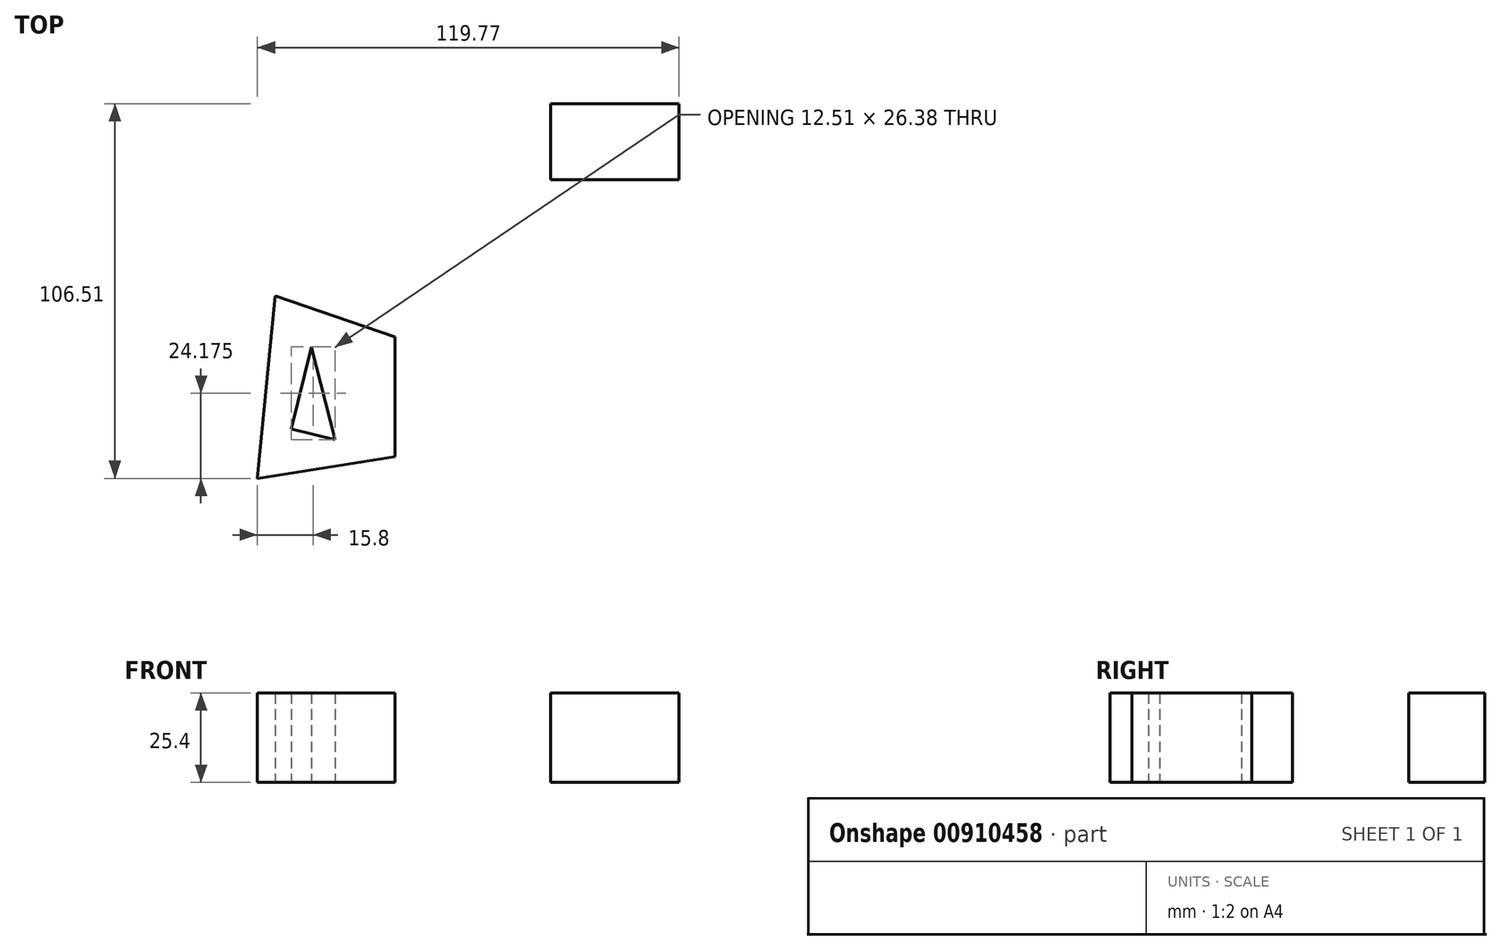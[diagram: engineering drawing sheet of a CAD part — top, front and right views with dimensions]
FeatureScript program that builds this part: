
annotation { "Feature Type Name" : "Feature", "Feature Type Description" : "" }
export const myFeature = defineFeature(function(context is Context, id is Id, definition is map)
    precondition{}
    {
        {
            var Q0;
            Q0=qCreatedBy(makeId("Top.planeOp"),FACE);
            var sketch = newSketch(context, id + "F0", { "sketchPlane" : qUnion([Q0])});
            skCircle(sketch, "E0", {"center": v(-62.28, 52.52) * mm, "radius": 11.18 * mm});
            skLineSegment(sketch, "E1.bottom", {"start": v(23.25, 37.16) * mm, "end": v(59.79, 37.16) * mm});
            skLineSegment(sketch, "E1.top", {"start": v(23.25, 15.57) * mm, "end": v(59.79, 15.57) * mm});
            skLineSegment(sketch, "E1.left", {"start": v(23.25, 37.16) * mm, "end": v(23.25, 15.57) * mm});
            skLineSegment(sketch, "E1.right", {"start": v(59.79, 37.16) * mm, "end": v(59.79, 15.57) * mm});
            skLineSegment(sketch, "E2", {"start": v(-55, -17.45) * mm, "end": v(-20.95, -29.08) * mm});
            skLineSegment(sketch, "E3", {"start": v(-20.95, -29.08) * mm, "end": v(-20.95, -63.13) * mm});
            skLineSegment(sketch, "E4", {"start": v(-20.95, -63.13) * mm, "end": v(-59.98, -69.35) * mm});
            skLineSegment(sketch, "E5", {"start": v(-59.98, -69.35) * mm, "end": v(-55, -17.45) * mm});
            skLineSegment(sketch, "E6", {"start": v(-44.62, -31.99) * mm, "end": v(-50.43, -55.24) * mm});
            skLineSegment(sketch, "E7", {"start": v(-50.43, -55.24) * mm, "end": v(-37.93, -58.36) * mm});
            skLineSegment(sketch, "E8", {"start": v(-37.93, -58.36) * mm, "end": v(-44.62, -31.99) * mm});
            skLineSegment(sketch, "E9", {"start": v(-82.91, 71.7) * mm, "end": v(-82.91, 30.26) * mm, "construction": true});
            skSolve(sketch);
        }
        {
            var Q0;
            Q0=makeQuery(id+"F0.imprint","IMPRINT",FACE,{"disambiguationData":[TD([[makeQuery(id+"F0.imprint","IMPRINT",EDGE,{"derivedFrom":sQuery(id+"F0.wireOp",EDGE,"E2")}),-1.0]])]});
            extrude(context, id + "F1", {"entities" : qUnion([Q0]), "depth" : 25.4 * mm, "offsetDistance" : 25.4 * mm});
        }
        {
            var Q0;
            Q0=makeQuery(id+"F0.imprint","IMPRINT",FACE,{"disambiguationData":[TD([[makeQuery(id+"F0.imprint","IMPRINT",EDGE,{"derivedFrom":sQuery(id+"F0.wireOp",EDGE,"E1.bottom")}),-1.0]])]});
            extrude(context, id + "F2", {"entities" : qUnion([Q0]), "depth" : 25.4 * mm, "offsetDistance" : 25.4 * mm});
        }
    });
